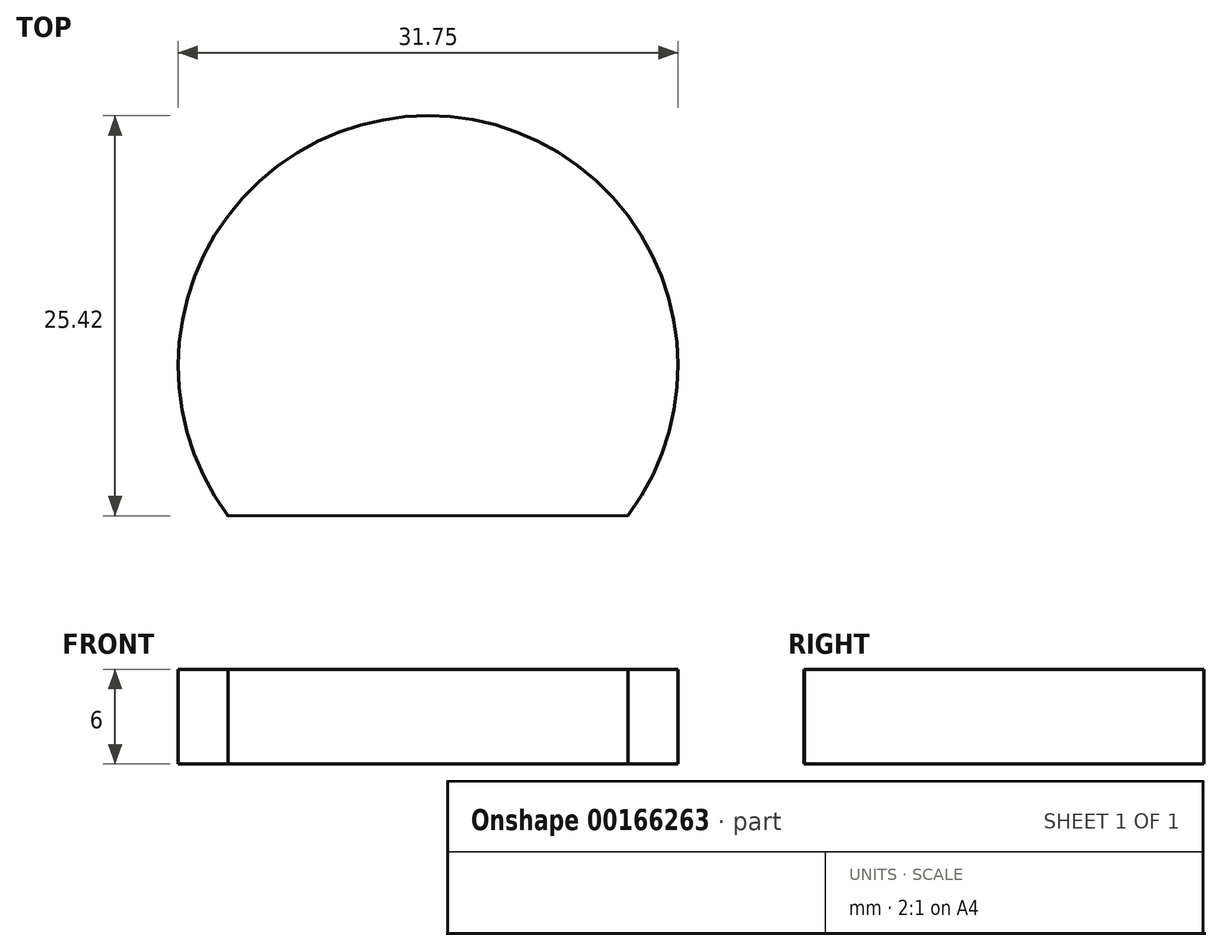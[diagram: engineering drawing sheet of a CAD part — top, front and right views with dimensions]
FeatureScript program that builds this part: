
annotation { "Feature Type Name" : "Feature", "Feature Type Description" : "" }
export const myFeature = defineFeature(function(context is Context, id is Id, definition is map)
    precondition{}
    {
        {
            var Q0;
            Q0=qCreatedBy(makeId("Top.planeOp"),FACE);
            var sketch = newSketch(context, id + "F0", { "sketchPlane" : qUnion([Q0])});
            skArc(sketch, "E0", {"start": v(-12.7, -9.54) * mm, "mid": v(-0.02, 15.87) * mm, "end": v(12.7, -9.51) * mm});
            skLineSegment(sketch, "E1", {"start": v(-12.7, -9.54) * mm, "end": v(12.7, -9.51) * mm});
            skSolve(sketch);
        }
        {
            var Q0;
            Q0 = qSketchRegion(id + "F0", true);
            extrude(context, id + "F1", {"entities" : qUnion([Q0]), "depth" : 6 * mm});
        }
    });
